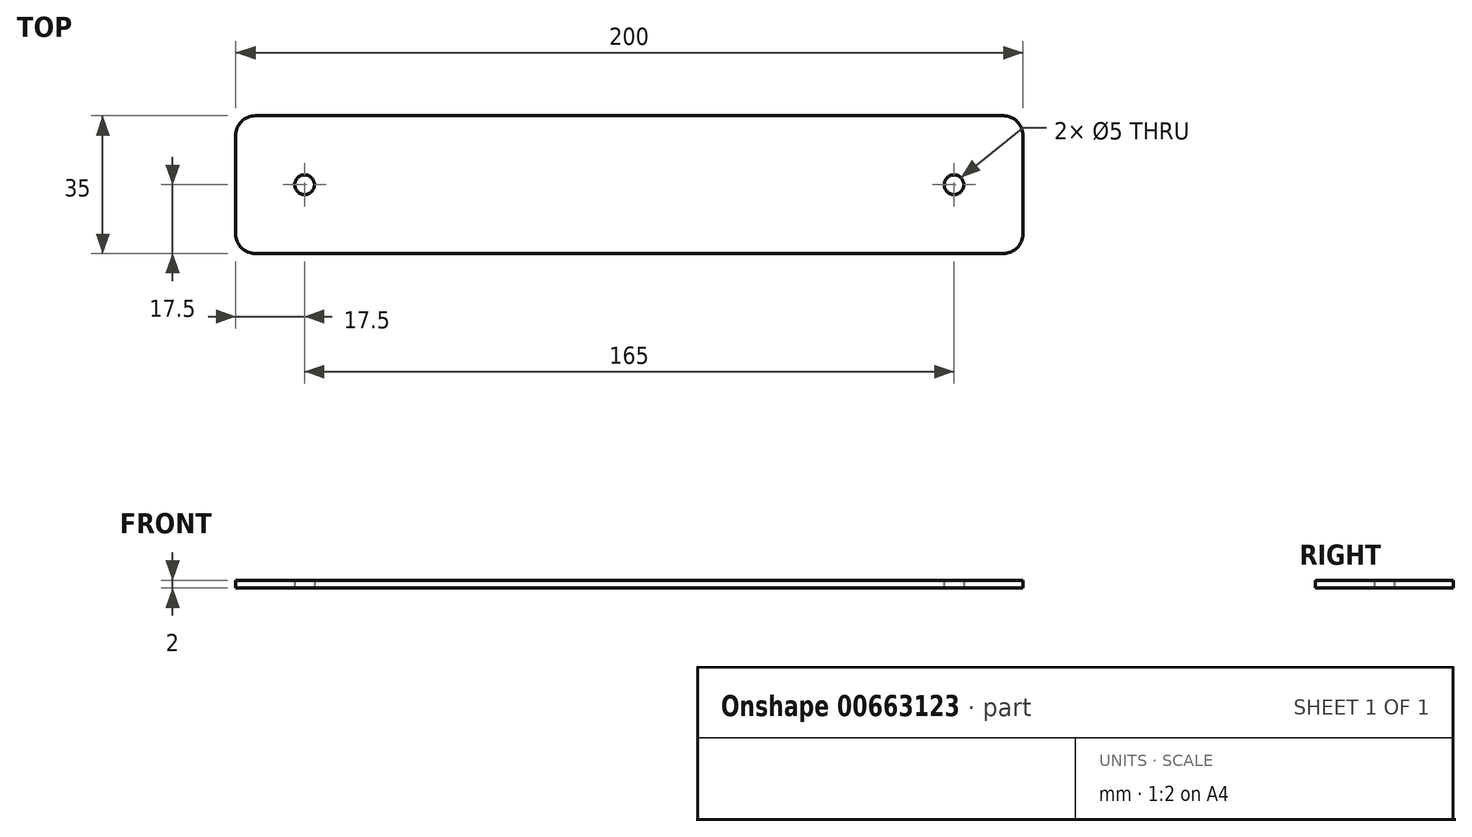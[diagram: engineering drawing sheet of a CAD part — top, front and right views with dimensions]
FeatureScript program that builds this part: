
annotation { "Feature Type Name" : "Feature", "Feature Type Description" : "" }
export const myFeature = defineFeature(function(context is Context, id is Id, definition is map)
    precondition{}
    {
        {
            var Q0;
            Q0=qCreatedBy(makeId("Top.planeOp"),FACE);
            var sketch = newSketch(context, id + "F0", { "sketchPlane" : qUnion([Q0])});
            skLineSegment(sketch, "E0.bottom", {"start": v(0, 0) * mm, "end": v(200, 0) * mm});
            skLineSegment(sketch, "E0.top", {"start": v(0, 35) * mm, "end": v(200, 35) * mm});
            skLineSegment(sketch, "E0.left", {"start": v(0, 0) * mm, "end": v(0, 35) * mm});
            skLineSegment(sketch, "E0.right", {"start": v(200, 0) * mm, "end": v(200, 35) * mm});
            skCircle(sketch, "E1", {"center": v(17.5, 17.5) * mm, "radius": 2.5 * mm});
            skPoint(sketch, "E1.centerSnap0", {"position": v(0, 17.5) * mm});
            skCircle(sketch, "E2", {"center": v(182.5, 17.5) * mm, "radius": 2.5 * mm});
            skPoint(sketch, "E2.centerSnap0", {"position": v(200, 17.5) * mm});
            skSolve(sketch);
        }
        {
            var Q0;
            Q0=makeQuery(id+"F0.imprint","IMPRINT",FACE,{"disambiguationData":[TD([[makeQuery(id+"F0.imprint","IMPRINT",EDGE,{"derivedFrom":sQuery(id+"F0.wireOp",EDGE,"E0.bottom")}),1.0]])]});
            extrude(context, id + "F1", {"entities" : qUnion([Q0]), "depth" : 2 * mm, "offsetDistance" : 25 * mm});
        }
        {
            var Q0;
            Q0=makeQuery(id+"F1.opExtrude","SWEPT_EDGE",EDGE,{"disambiguationData":[OSD([sQuery(id+"F0.wireOp",EDGE,"E0.bottom"),sQuery(id+"F0.wireOp",EDGE,"E0.left")])]});
            var Q1;
            Q1=makeQuery(id+"F1.opExtrude","SWEPT_EDGE",EDGE,{"disambiguationData":[OSD([sQuery(id+"F0.wireOp",EDGE,"E0.top"),sQuery(id+"F0.wireOp",EDGE,"E0.left")])]});
            var Q2;
            Q2=makeQuery(id+"F1.opExtrude","SWEPT_EDGE",EDGE,{"disambiguationData":[OSD([sQuery(id+"F0.wireOp",EDGE,"E0.top"),sQuery(id+"F0.wireOp",EDGE,"E0.right")])]});
            var Q3;
            Q3=makeQuery(id+"F1.opExtrude","SWEPT_EDGE",EDGE,{"disambiguationData":[OSD([sQuery(id+"F0.wireOp",EDGE,"E0.bottom"),sQuery(id+"F0.wireOp",EDGE,"E0.right")])]});
            fillet(context, id + "F2", {"entities" : qUnion([Q0, Q1, Q2, Q3]), "radius" : 5 * mm, "tangentPropagation" : true, "allowEdgeOverflow" : false});
        }
    });
